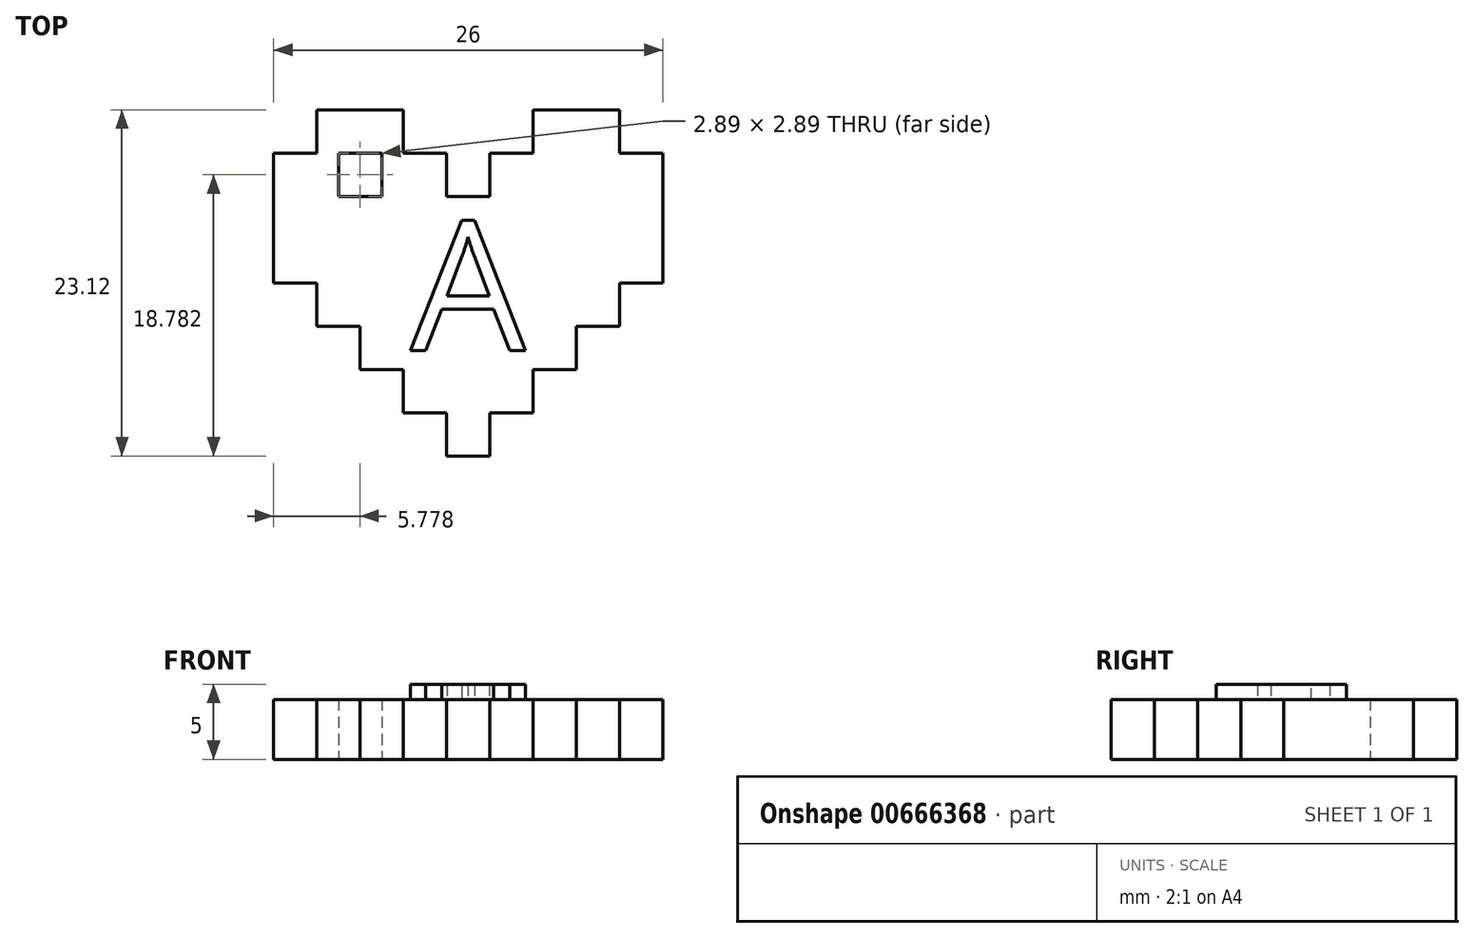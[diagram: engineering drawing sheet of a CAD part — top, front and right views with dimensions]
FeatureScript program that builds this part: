
annotation { "Feature Type Name" : "Feature", "Feature Type Description" : "" }
export const myFeature = defineFeature(function(context is Context, id is Id, definition is map)
    precondition{}
    {
        {
            var Q0;
            Q0=qCreatedBy(makeId("Top.planeOp"),FACE);
            var sketch = newSketch(context, id + "F0", { "sketchPlane" : qUnion([Q0])});
            skLineSegment(sketch, "E0", {"start": v(-13, 0) * mm, "end": v(-13, 8.67) * mm});
            skLineSegment(sketch, "E1", {"start": v(-13, 8.67) * mm, "end": v(-10.11, 8.67) * mm});
            skLineSegment(sketch, "E2", {"start": v(-10.11, 8.67) * mm, "end": v(-10.11, 11.56) * mm});
            skLineSegment(sketch, "E3", {"start": v(-10.11, 11.56) * mm, "end": v(-4.33, 11.56) * mm});
            skLineSegment(sketch, "E4", {"start": v(-4.33, 11.56) * mm, "end": v(-4.33, 8.67) * mm});
            skLineSegment(sketch, "E5", {"start": v(-4.33, 8.67) * mm, "end": v(-1.44, 8.67) * mm});
            skLineSegment(sketch, "E6", {"start": v(-1.44, 8.67) * mm, "end": v(-1.44, 5.78) * mm});
            skLineSegment(sketch, "E7", {"start": v(-1.44, 5.78) * mm, "end": v(1.44, 5.78) * mm});
            skLineSegment(sketch, "E8", {"start": v(1.44, 5.78) * mm, "end": v(1.44, 8.67) * mm});
            skLineSegment(sketch, "E9", {"start": v(1.44, 8.67) * mm, "end": v(4.33, 8.67) * mm});
            skLineSegment(sketch, "E10", {"start": v(4.33, 8.67) * mm, "end": v(4.33, 11.56) * mm});
            skLineSegment(sketch, "E11", {"start": v(4.33, 11.56) * mm, "end": v(10.11, 11.56) * mm});
            skLineSegment(sketch, "E12", {"start": v(10.11, 11.56) * mm, "end": v(10.11, 8.67) * mm});
            skLineSegment(sketch, "E13", {"start": v(10.11, 8.67) * mm, "end": v(13, 8.67) * mm});
            skLineSegment(sketch, "E14", {"start": v(13, 8.67) * mm, "end": v(13, 0) * mm});
            skLineSegment(sketch, "E15", {"start": v(13, 0) * mm, "end": v(10.11, 0) * mm});
            skLineSegment(sketch, "E16", {"start": v(10.11, 0) * mm, "end": v(10.11, -2.89) * mm});
            skLineSegment(sketch, "E17", {"start": v(10.11, -2.89) * mm, "end": v(7.22, -2.89) * mm});
            skLineSegment(sketch, "E18", {"start": v(7.22, -2.89) * mm, "end": v(7.22, -5.78) * mm});
            skLineSegment(sketch, "E19", {"start": v(7.22, -5.78) * mm, "end": v(4.33, -5.78) * mm});
            skLineSegment(sketch, "E20", {"start": v(4.33, -5.78) * mm, "end": v(4.33, -8.67) * mm});
            skLineSegment(sketch, "E21", {"start": v(4.33, -8.67) * mm, "end": v(1.44, -8.67) * mm});
            skLineSegment(sketch, "E22", {"start": v(1.44, -8.67) * mm, "end": v(1.44, -11.56) * mm});
            skLineSegment(sketch, "E23", {"start": v(1.44, -11.56) * mm, "end": v(-1.44, -11.56) * mm});
            skLineSegment(sketch, "E24", {"start": v(-1.44, -11.56) * mm, "end": v(-1.44, -8.67) * mm});
            skLineSegment(sketch, "E25", {"start": v(-1.44, -8.67) * mm, "end": v(-4.33, -8.67) * mm});
            skLineSegment(sketch, "E26", {"start": v(-4.33, -8.67) * mm, "end": v(-4.33, -5.78) * mm});
            skLineSegment(sketch, "E27", {"start": v(-4.33, -5.78) * mm, "end": v(-7.22, -5.78) * mm});
            skLineSegment(sketch, "E28", {"start": v(-7.22, -5.78) * mm, "end": v(-7.22, -2.89) * mm});
            skLineSegment(sketch, "E29", {"start": v(-7.22, -2.89) * mm, "end": v(-10.11, -2.89) * mm});
            skLineSegment(sketch, "E30", {"start": v(-10.11, -2.89) * mm, "end": v(-10.11, 0) * mm});
            skLineSegment(sketch, "E31", {"start": v(-10.11, 0) * mm, "end": v(-13, 0) * mm});
            skLineSegment(sketch, "E32", {"start": v(-8.67, 5.78) * mm, "end": v(-8.67, 8.67) * mm});
            skLineSegment(sketch, "E33", {"start": v(-8.67, 8.67) * mm, "end": v(-5.78, 8.67) * mm});
            skLineSegment(sketch, "E34", {"start": v(-5.78, 8.67) * mm, "end": v(-5.78, 5.78) * mm});
            skLineSegment(sketch, "E35", {"start": v(-5.78, 5.78) * mm, "end": v(-8.67, 5.78) * mm});
            skSolve(sketch);
        }
        {
            var Q0;
            Q0 = qSketchRegion(id + "F0", true);
            var Q1;
            Q1=makeQuery(id+"F0.imprint","IMPRINT",FACE,{"disambiguationData":[TD([[makeQuery(id+"F0.imprint","IMPRINT",EDGE,{"derivedFrom":sQuery(id+"F0.wireOp",EDGE,"ec0dd8b7-1967-4a6f-a451-ef337cbacd9a.sketch_text.stroke-8")}),1.0]])]});
            var Q2;
            Q2=makeQuery(id+"F0.imprint","IMPRINT",FACE,{"disambiguationData":[TD([[makeQuery(id+"F0.imprint","IMPRINT",EDGE,{"derivedFrom":sQuery(id+"F0.wireOp",EDGE,"ec0dd8b7-1967-4a6f-a451-ef337cbacd9a.sketch_text.stroke-0")}),1.0]])]});
            var Q3;
            Q3=makeQuery(id+"F0.imprint","IMPRINT",FACE,{"disambiguationData":[TD([[makeQuery(id+"F0.imprint","IMPRINT",EDGE,{"derivedFrom":sQuery(id+"F0.wireOp",EDGE,"ec0dd8b7-1967-4a6f-a451-ef337cbacd9a.sketch_text.stroke-0")}),-1.0]])]});
            extrude(context, id + "F1", {"entities" : qUnion([Q0, Q1, Q2, Q3]), "depth" : 4 * mm, "offsetDistance" : 25.4 * mm});
        }
        {
            var Q0;
            Q0=makeQuery(id+"F0.imprint","IMPRINT",FACE,{"disambiguationData":[TD([[makeQuery(id+"F0.imprint","IMPRINT",EDGE,{"derivedFrom":sQuery(id+"F0.wireOp",EDGE,"E0")}),-1.0]])]});
            var sketch = newSketch(context, id + "F2", { "sketchPlane" : qUnion([Q0])});
            skText(sketch, "E36", { "text": "A", "fontName": "OpenSans-Regular.ttf"});
            const initialGuessF2  = {"E36": [-0.00385, -0.00452, 1, 0, 0.00874]};
            skSetInitialGuess(sketch, initialGuessF2);
            skSolve(sketch);
        }
        {
            var Q0;
            Q0 = qSketchRegion(id + "F2", true);
            extrude(context, id + "F3", {"entities" : qUnion([Q0]), "operationType" : NewBodyOperationType.ADD, "depth" : 5 * mm, "offsetDistance" : 25 * mm});
        }
    });
